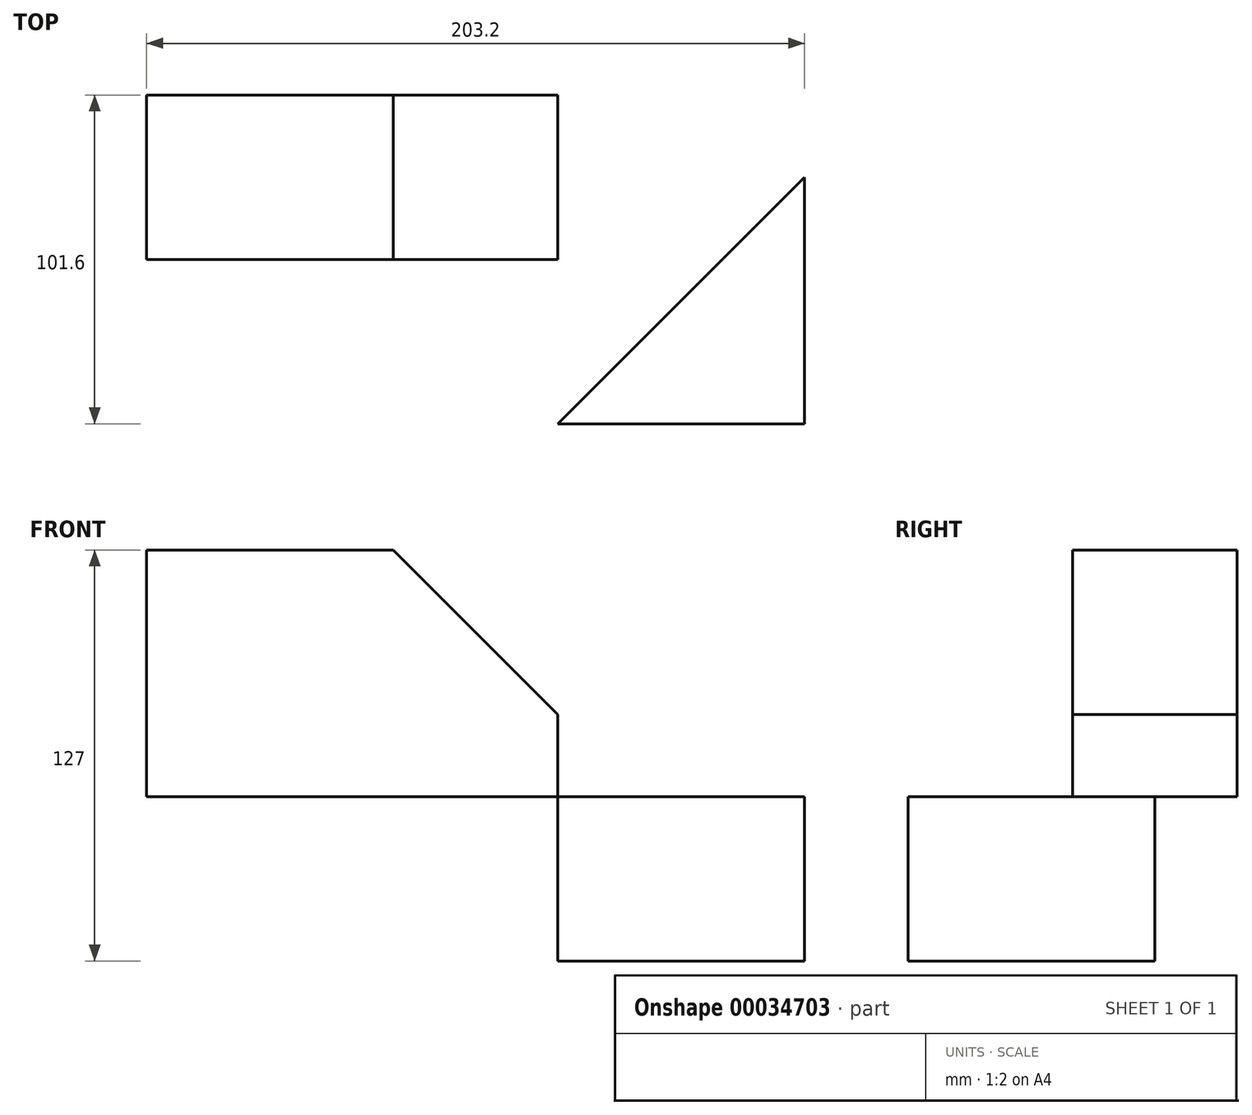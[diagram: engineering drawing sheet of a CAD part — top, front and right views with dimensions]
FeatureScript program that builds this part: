
annotation { "Feature Type Name" : "Feature", "Feature Type Description" : "" }
export const myFeature = defineFeature(function(context is Context, id is Id, definition is map)
    precondition{}
    {
        {
            var Q0;
            Q0=qCreatedBy(makeId("Top.planeOp"),FACE);
            var sketch = newSketch(context, id + "F0", { "sketchPlane" : qUnion([Q0])});
            skLineSegment(sketch, "E0.bottom", {"start": v(-65.57, -76.2) * mm, "end": v(137.63, -76.2) * mm});
            skLineSegment(sketch, "E0.top", {"start": v(-65.57, 25.4) * mm, "end": v(137.63, 25.4) * mm});
            skLineSegment(sketch, "E0.left", {"start": v(-65.57, -76.2) * mm, "end": v(-65.57, 25.4) * mm});
            skLineSegment(sketch, "E0.right", {"start": v(137.63, -76.2) * mm, "end": v(137.63, 25.4) * mm});
            skLineSegment(sketch, "E1", {"start": v(137.63, 25.4) * mm, "end": v(137.63, 0) * mm});
            skLineSegment(sketch, "E2", {"start": v(137.63, 0) * mm, "end": v(137.63, -76.2) * mm});
            skLineSegment(sketch, "E3", {"start": v(137.63, -76.2) * mm, "end": v(61.43, -76.2) * mm});
            skLineSegment(sketch, "E4", {"start": v(61.43, -76.2) * mm, "end": v(137.63, 0) * mm});
            skSolve(sketch);
        }
        {
            var Q0;
            Q0=makeQuery(id+"F0.imprint","IMPRINT",FACE,{"disambiguationData":[TD([[makeQuery(id+"F0.imprint","IMPRINT",EDGE,{"derivedFrom":sQuery(id+"F0.wireOp",EDGE,"E0.bottom")}),1.0]])]});
            extrude(context, id + "F1", {"entities" : qUnion([Q0]), "depth" : 50.8 * mm});
        }
        {
            var Q0;
            Q0=makeQuery(id+"F1.opExtrude","CAP_FACE",FACE,{"disambiguationData":[OSD([sQuery(id+"F0.wireOp",EDGE,"E0.bottom"),sQuery(id+"F0.wireOp",EDGE,"E0.top"),sQuery(id+"F0.wireOp",EDGE,"E0.left"),sQuery(id+"F0.wireOp",EDGE,"E1"),sQuery(id+"F0.wireOp",EDGE,"E4")])],"isStart":false});
            var sketch = newSketch(context, id + "F2", { "sketchPlane" : qUnion([Q0])});
            skLineSegment(sketch, "E5.bottom", {"start": v(-65.57, 25.4) * mm, "end": v(61.43, 25.4) * mm});
            skLineSegment(sketch, "E5.top", {"start": v(-65.57, -25.4) * mm, "end": v(61.43, -25.4) * mm});
            skLineSegment(sketch, "E5.left", {"start": v(-65.57, 25.4) * mm, "end": v(-65.57, -25.4) * mm});
            skLineSegment(sketch, "E5.right", {"start": v(61.43, 25.4) * mm, "end": v(61.43, -25.4) * mm});
            skSolve(sketch);
        }
        {
            var Q0;
            Q0=makeQuery(id+"F2.imprint","IMPRINT",FACE,{"disambiguationData":[TD([[makeQuery(id+"F2.imprint","IMPRINT",EDGE,{"derivedFrom":sQuery(id+"F2.wireOp",EDGE,"E5.bottom")}),-1.0]])]});
            extrude(context, id + "F3", {"entities" : qUnion([Q0]), "operationType" : NewBodyOperationType.ADD, "depth" : 76.2 * mm});
        }
        {
            var Q0;
            Q0=makeQuery(id+"F3.opExtrude","CAP_EDGE",EDGE,{"disambiguationData":[OSD([sQuery(id+"F2.wireOp",EDGE,"E5.right")])],"isStart":false});
            chamfer(context, id + "F4", {"entities" : qUnion([Q0]), "width" : 50.8 * mm, "tangentPropagation" : true});
        }
    });
